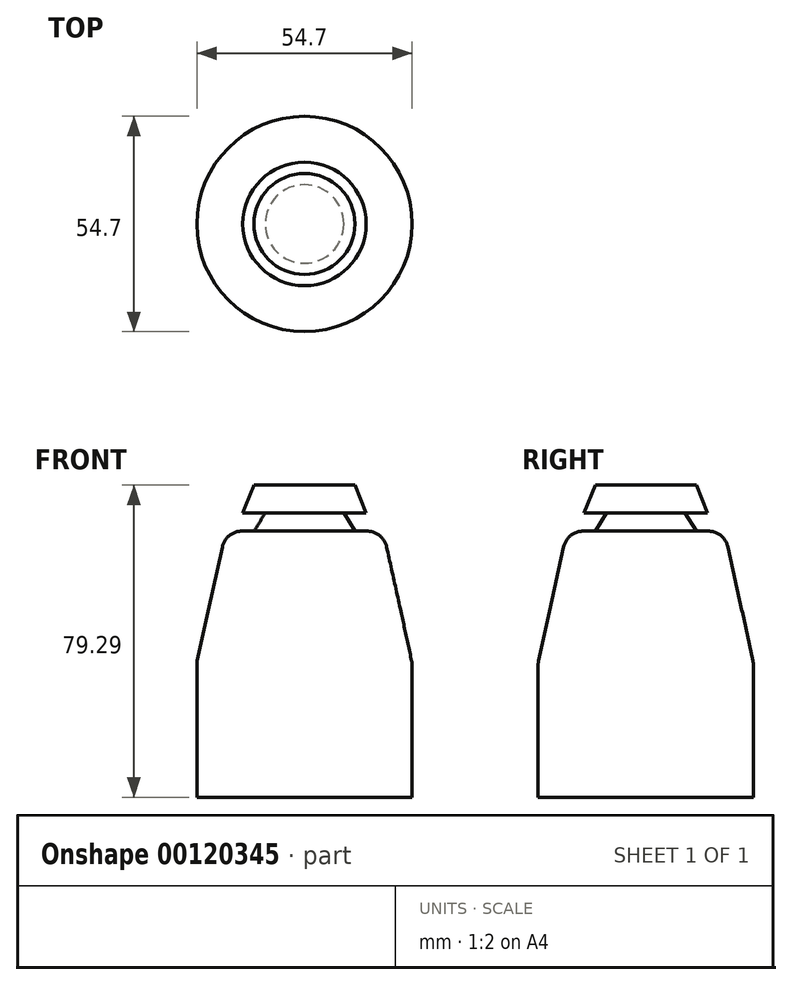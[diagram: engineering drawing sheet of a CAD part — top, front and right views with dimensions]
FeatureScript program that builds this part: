
annotation { "Feature Type Name" : "Feature", "Feature Type Description" : "" }
export const myFeature = defineFeature(function(context is Context, id is Id, definition is map)
    precondition{}
    {
        {
            var Q0;
            Q0=qCreatedBy(makeId("Front.planeOp"),FACE);
            var sketch = newSketch(context, id + "F0", { "sketchPlane" : qUnion([Q0])});
            skLineSegment(sketch, "E0", {"start": v(0, 28.95) * mm, "end": v(-12.84, 28.95) * mm});
            skLineSegment(sketch, "E1", {"start": v(-12.84, 28.95) * mm, "end": v(-15.69, 21.82) * mm});
            skLineSegment(sketch, "E2", {"start": v(-15.69, 21.82) * mm, "end": v(-9.98, 21.82) * mm});
            skLineSegment(sketch, "E3", {"start": v(-9.98, 21.82) * mm, "end": v(-12.84, 17.26) * mm});
            skLineSegment(sketch, "E4", {"start": v(-12.84, 17.26) * mm, "end": v(-19.97, 17.26) * mm});
            skLineSegment(sketch, "E5", {"start": v(-19.97, 17.26) * mm, "end": v(-24.5, -3.18) * mm});
            skLineSegment(sketch, "E6", {"start": v(-24.5, -3.18) * mm, "end": v(-21.83, -3.18) * mm});
            skLineSegment(sketch, "E7", {"start": v(-24.5, -3.18) * mm, "end": v(-27.35, -16.27) * mm});
            skLineSegment(sketch, "E8", {"start": v(-27.35, -16.27) * mm, "end": v(-27.35, -50.34) * mm});
            skLineSegment(sketch, "E9", {"start": v(-27.35, -50.34) * mm, "end": v(0, -50.34) * mm});
            skLineSegment(sketch, "E10", {"start": v(0, -50.34) * mm, "end": v(0, 28.95) * mm});
            skSolve(sketch);
        }
        {
            var Q0;
            Q0 = qSketchRegion(id + "F0", true);
            var Q1;
            Q1=sQuery(id+"F0.wireOp",EDGE,"E10");
            revolve(context, id + "F1", {"entities" : qUnion([Q0]), "axis" : qUnion([Q1]), "revolveType" : RevolveType.FULL});
        }
        {
            var Q0;
            Q0=makeQuery(id+"F1.opRevolve","SWEPT_FACE",FACE,{"disambiguationData":[OSD([sQuery(id+"F0.wireOp",EDGE,"E5")])]});
            fillet(context, id + "F2", {"entities" : qUnion([Q0]), "radius" : 5.08 * mm, "tangentPropagation" : true, "allowEdgeOverflow" : false});
        }
        {
            var Q0;
            Q0=makeQuery(id+"F1.opRevolve","SWEPT_EDGE",EDGE,{"disambiguationData":[OSD([sQuery(id+"F0.wireOp",EDGE,"E7"),sQuery(id+"F0.wireOp",EDGE,"E8")])]});
            fillet(context, id + "F3", {"entities" : qUnion([Q0]), "radius" : 5.08 * mm, "tangentPropagation" : true, "allowEdgeOverflow" : false});
        }
    });
